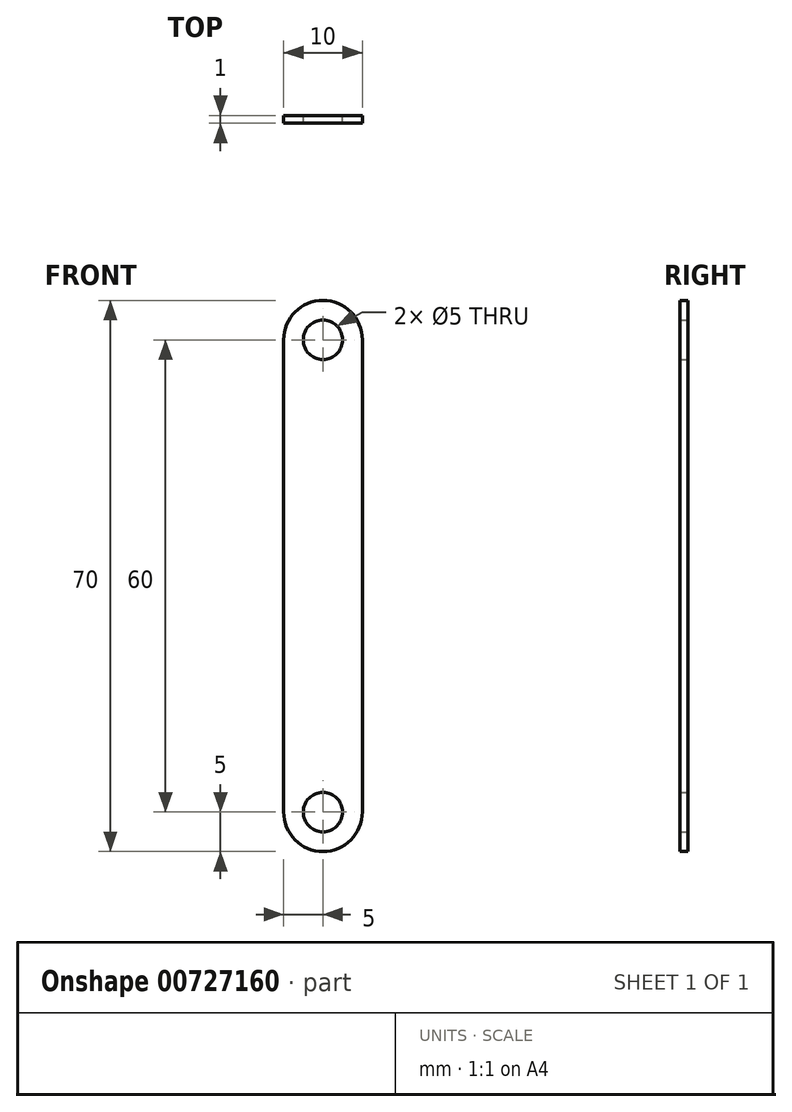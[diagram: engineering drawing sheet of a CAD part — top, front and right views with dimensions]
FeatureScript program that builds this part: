
annotation { "Feature Type Name" : "Feature", "Feature Type Description" : "" }
export const myFeature = defineFeature(function(context is Context, id is Id, definition is map)
    precondition{}
    {
        {
            var Q0;
            Q0=qCreatedBy(makeId("Front.planeOp"),FACE);
            var sketch = newSketch(context, id + "F0", { "sketchPlane" : qUnion([Q0])});
            skArc(sketch, "E0", {"start": v(5, 30) * mm, "mid": v(0, 35) * mm, "end": v(-5, 30) * mm});
            skArc(sketch, "E1", {"start": v(-5, -30) * mm, "mid": v(0, -35) * mm, "end": v(5, -30) * mm});
            skCircle(sketch, "E2", {"center": v(0, -30) * mm, "radius": 2.5 * mm});
            skCircle(sketch, "E3", {"center": v(0, 30) * mm, "radius": 2.5 * mm});
            skLineSegment(sketch, "E4", {"start": v(5, 30) * mm, "end": v(5, -30) * mm});
            skLineSegment(sketch, "E5", {"start": v(-5, -30) * mm, "end": v(-5, 30) * mm});
            skSolve(sketch);
        }
        {
            var Q0;
            Q0 = qSketchRegion(id + "F0", true);
            extrude(context, id + "F1", {"entities" : qUnion([Q0]), "depth" : 1 * mm, "offsetDistance" : 25.4 * mm});
        }
    });
